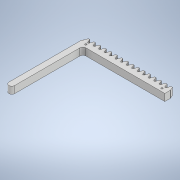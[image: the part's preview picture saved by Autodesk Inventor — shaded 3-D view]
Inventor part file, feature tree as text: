
AUTODESK INVENTOR PART (.ipt)
format: ipt  version: 2021 (Build 250183000, 183)  size: 229,376 bytes
history: native  units: in
note: dims shown in document units (in); Inventor stores cm internally (conversion verified against a paired STEP export)
features: extrude x2, fillet x2, sketch x2
ambient origin geometry x8: Origin, YZ Plane, XZ Plane, XY Plane, X Axis, Y Axis, Z Axis, Center Point
bodies: Solid1 (feature_tree), Solid2 (feature_tree)
feature tree (6):
  extrude  "Extrusion4"  Depth=0.1969in
  fillet  "Fillet1"  Radius=0.3937in
  fillet  "Fillet2"  Radius=0.1969in
  extrude  "Extrusion6"  Depth=0.3937in
  sketch  "Sketch4"  dims[d14=0.4724in d15=5.1378in d16=0.3937in d17=0.0in d21=0.1969in]
  sketch  "Sketch6"  dims[d22=0.1969in d23=0.1181in d24=0.1181in d25=0.1969in d26=0.1969in d27=0.3937in d28=0.3937in d29=0.0in d30=0.0in d3=0.0197in d4=1.9685in d5=0.0197in d6=1.9685in]
